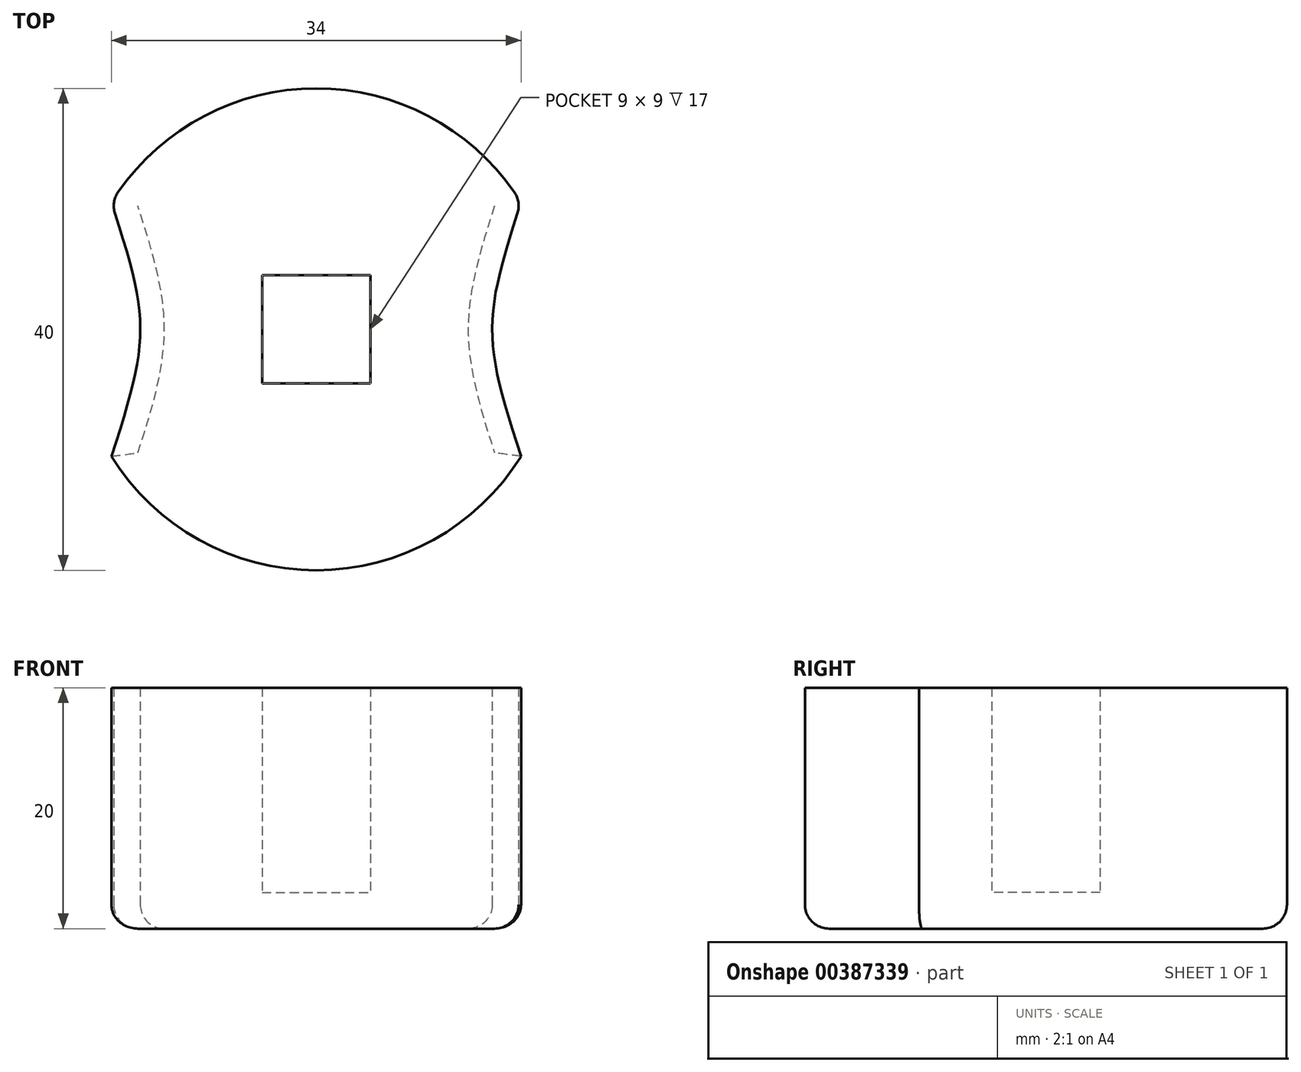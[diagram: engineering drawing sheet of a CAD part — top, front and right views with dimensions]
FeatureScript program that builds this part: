
annotation { "Feature Type Name" : "Feature", "Feature Type Description" : "" }
export const myFeature = defineFeature(function(context is Context, id is Id, definition is map)
    precondition{}
    {
        {
            var Q0;
            Q0=qCreatedBy(makeId("Top.planeOp"),FACE);
            var sketch = newSketch(context, id + "F0", { "sketchPlane" : qUnion([Q0])});
            skCircle(sketch, "E0", {"center": v(0, 0) * mm, "radius": 20 * mm});
            skLineSegment(sketch, "E1.bottom", {"start": v(4.5, -4.5) * mm, "end": v(-4.5, -4.5) * mm});
            skLineSegment(sketch, "E1.top", {"start": v(4.5, 4.5) * mm, "end": v(-4.5, 4.5) * mm});
            skLineSegment(sketch, "E1.left", {"start": v(4.5, -4.5) * mm, "end": v(4.5, 4.5) * mm});
            skLineSegment(sketch, "E1.right", {"start": v(-4.5, -4.5) * mm, "end": v(-4.5, 4.5) * mm});
            skLineSegment(sketch, "E2", {"start": v(0, -0.75) * mm, "end": v(0, -24.81) * mm, "construction": true});
            skLineSegment(sketch, "E3", {"start": v(-17, -21.46) * mm, "end": v(-17, 22.13) * mm, "construction": true});
            skFitSpline(sketch, "E4", {"points": [v(-17, -10.54) * mm, v(-14.6, 0) * mm, v(-17, 10.54) * mm], "startDerivative": vector(9.37, 28.57) * mm, "endDerivative": vector(-9.37, 28.57) * mm});
            skFitSpline(sketch, "E5.MirrorCS", {"points": [v(17, -10.54) * mm, v(14.6, 0) * mm, v(17, 10.54) * mm], "startDerivative": vector(-9.37, 28.57) * mm, "endDerivative": vector(9.37, 28.57) * mm});
            skSolve(sketch);
        }
        {
            var Q0;
            Q0=qSketchRegion(id+"F0",true);
            var Q1;
            Q1=makeQuery(id+"F0.imprint","IMPRINT",FACE,{"disambiguationData":[TD([[makeQuery(id+"F0.imprint","IMPRINT",EDGE,{"derivedFrom":sQuery(id+"F0.wireOp",EDGE,"E1.bottom")}),-1.0]])]});
            extrude(context, id + "F1", {"entities" : qUnion([Q0, Q1]), "depth" : 3 * mm});
        }
        {
            var Q0;
            Q0=makeQuery(id+"F0.imprint","IMPRINT",FACE,{"disambiguationData":[TD([[makeQuery(id+"F0.imprint","IMPRINT",EDGE,{"derivedFrom":sQuery(id+"F0.wireOp",EDGE,"E0")}),1.0]])]});
            extrude(context, id + "F2", {"entities" : qUnion([Q0]), "operationType" : NewBodyOperationType.ADD, "depth" : 20 * mm});
        }
        {
            var Q0;
            {var subQ0=sQuery(id+"F0.wireOp",EDGE,"E4");Q0=makeQuery(id+"F0.imprint","IMPRINT",FACE,{"disambiguationData":[TD([[makeQuery(id+"F0.imprint","IMPRINT",EDGE,{"derivedFrom":subQ0}),1.0]])]});}
            var Q1;
            {var subQ0=sQuery(id+"F0.wireOp",EDGE,"E5.MirrorCS");Q1=makeQuery(id+"F0.imprint","IMPRINT",FACE,{"disambiguationData":[TD([[makeQuery(id+"F0.imprint","IMPRINT",EDGE,{"derivedFrom":subQ0}),-1.0]])]});}
            extrude(context, id + "F3", {"entities" : qUnion([Q0, Q1]), "operationType" : NewBodyOperationType.REMOVE, "depth" : 25 * mm});
        }
        {
            var Q0;
            Q0=makeQuery(id+"F1.opExtrude","CAP_FACE",FACE,{"disambiguationData":[OSD([sQuery(id+"F0.wireOp",EDGE,"E0")])],"isStart":true});
            var Q1;
            {var subQ0=sQuery(id+"F0.wireOp",EDGE,"E4");var subQ1=sQuery(id+"F0.wireOp",EDGE,"E0");Q1=makeQuery(id+"F3.boolean.opBoolean","COPY",EDGE,{"derivedFrom":makeQuery(id+"F3.opExtrude","SWEPT_EDGE",EDGE,{"disambiguationData":[OSD([subQ1,subQ0]),TDD([makeQuery(id+"F0.imprint","INTERSECT",VERTEX,{"disambiguationData":[OD(0.0)],"derivedFrom":[subQ1,subQ0]})])]})});}
            var Q2;
            {var subQ0=sQuery(id+"F0.wireOp",EDGE,"E4");var subQ1=sQuery(id+"F0.wireOp",EDGE,"E0");Q2=makeQuery(id+"F3.boolean.opBoolean","COPY",EDGE,{"derivedFrom":makeQuery(id+"F3.opExtrude","SWEPT_EDGE",EDGE,{"disambiguationData":[OSD([subQ1,subQ0]),TDD([makeQuery(id+"F0.imprint","INTERSECT",VERTEX,{"disambiguationData":[OD(1.0)],"derivedFrom":[subQ1,subQ0]})])]})});}
            var Q3;
            {var subQ0=sQuery(id+"F0.wireOp",EDGE,"E5.MirrorCS");var subQ1=sQuery(id+"F0.wireOp",EDGE,"E0");Q3=makeQuery(id+"F3.boolean.opBoolean","COPY",EDGE,{"derivedFrom":makeQuery(id+"F3.opExtrude","SWEPT_EDGE",EDGE,{"disambiguationData":[OSD([subQ1,subQ0]),TDD([makeQuery(id+"F0.imprint","INTERSECT",VERTEX,{"disambiguationData":[OD(0.0)],"derivedFrom":[subQ1,subQ0]})])]})});}
            var Q4;
            {var subQ0=sQuery(id+"F0.wireOp",EDGE,"E5.MirrorCS");var subQ1=sQuery(id+"F0.wireOp",EDGE,"E0");Q4=makeQuery(id+"F3.boolean.opBoolean","COPY",EDGE,{"derivedFrom":makeQuery(id+"F3.opExtrude","SWEPT_EDGE",EDGE,{"disambiguationData":[OSD([subQ1,subQ0]),TDD([makeQuery(id+"F0.imprint","INTERSECT",VERTEX,{"disambiguationData":[OD(1.0)],"derivedFrom":[subQ1,subQ0]})])]})});}
            fillet(context, id + "F4", {"entities" : qUnion([Q0, Q1, Q2, Q3, Q4]), "radius" : 2 * mm, "tangentPropagation" : true, "allowEdgeOverflow" : false});
        }
    });
